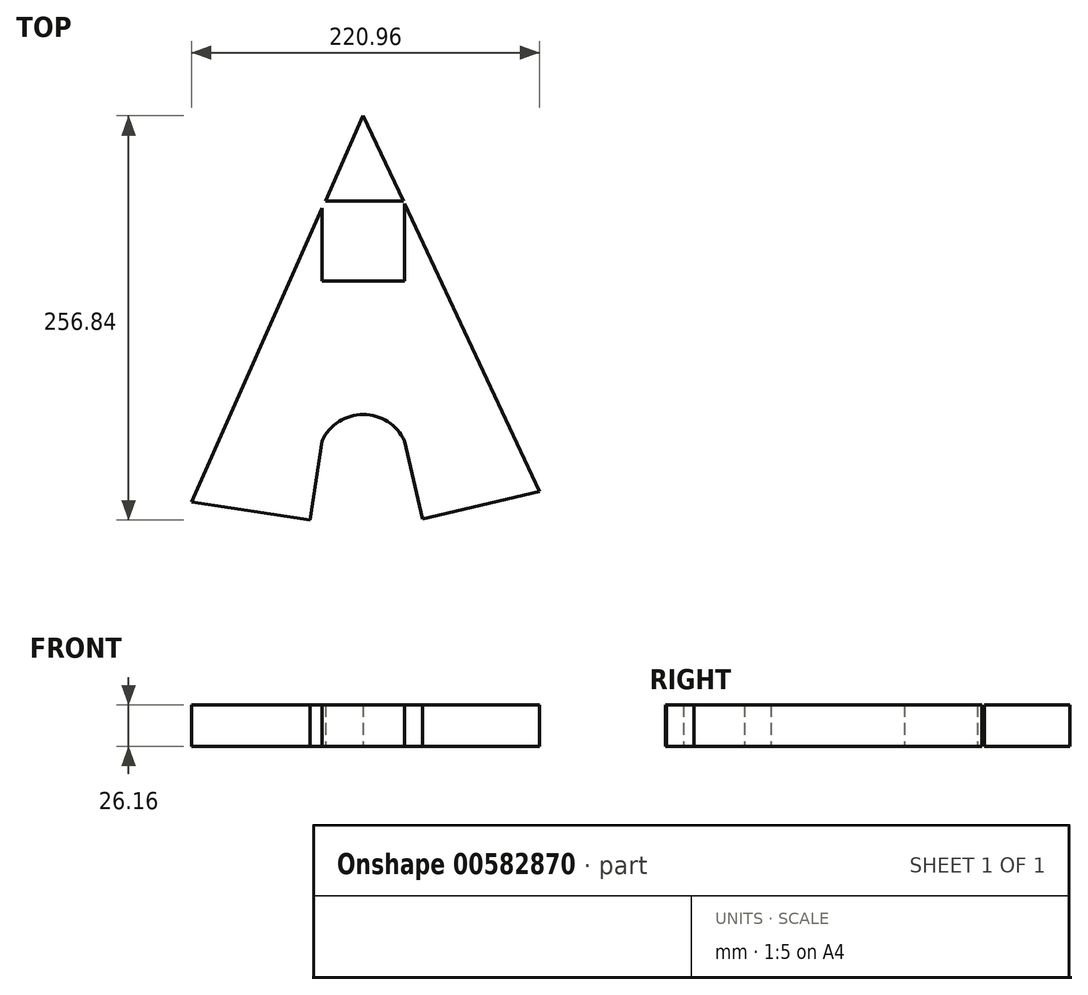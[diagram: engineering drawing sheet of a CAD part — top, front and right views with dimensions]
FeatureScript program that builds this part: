
annotation { "Feature Type Name" : "Feature", "Feature Type Description" : "" }
export const myFeature = defineFeature(function(context is Context, id is Id, definition is map)
    precondition{}
    {
        {
            var Q0;
            Q0=qCreatedBy(makeId("Top.planeOp"),FACE);
            var sketch = newSketch(context, id + "F0", { "sketchPlane" : qUnion([Q0])});
            skArc(sketch, "E0", {"start": v(52.24, 0) * mm, "mid": v(26.12, 16.74) * mm, "end": v(0, 0) * mm});
            skLineSegment(sketch, "E1", {"start": v(0, 0) * mm, "end": v(-7.57, -50.23) * mm});
            skLineSegment(sketch, "E2", {"start": v(0, 0) * mm, "end": v(0, 101.6) * mm});
            skLineSegment(sketch, "E3", {"start": v(52.24, 0) * mm, "end": v(63.87, -49.45) * mm});
            skLineSegment(sketch, "E4", {"start": v(52.24, 0) * mm, "end": v(52.24, 101.6) * mm});
            skLineSegment(sketch, "E5", {"start": v(52.24, 50.8) * mm, "end": v(0, 50.8) * mm});
            skLineSegment(sketch, "E6", {"start": v(0, 50.8) * mm, "end": v(52.24, 101.6) * mm});
            skLineSegment(sketch, "E7", {"start": v(0, 101.6) * mm, "end": v(52.24, 101.6) * mm});
            skLineSegment(sketch, "E8", {"start": v(0, 101.6) * mm, "end": v(52.24, 50.8) * mm});
            skLineSegment(sketch, "E9", {"start": v(0, 101.6) * mm, "end": v(0, 152.4) * mm});
            skLineSegment(sketch, "E10", {"start": v(0, 152.4) * mm, "end": v(52.24, 101.6) * mm});
            skLineSegment(sketch, "E11", {"start": v(0, 152.4) * mm, "end": v(52.24, 152.4) * mm});
            skLineSegment(sketch, "E12", {"start": v(52.24, 152.4) * mm, "end": v(52.24, 101.6) * mm});
            skLineSegment(sketch, "E13", {"start": v(52.24, 152.4) * mm, "end": v(0, 101.6) * mm});
            skLineSegment(sketch, "E14", {"start": v(0, 152.4) * mm, "end": v(26.12, 206.6) * mm});
            skPoint(sketch, "E14.endSnap0", {"position": v(26.12, 152.4) * mm});
            skLineSegment(sketch, "E15", {"start": v(26.12, 206.6) * mm, "end": v(52.24, 152.4) * mm});
            skLineSegment(sketch, "E16", {"start": v(-7.57, -50.23) * mm, "end": v(-82.92, -38.88) * mm});
            skLineSegment(sketch, "E17", {"start": v(-82.92, -38.88) * mm, "end": v(26.12, 206.6) * mm});
            skLineSegment(sketch, "E18", {"start": v(63.87, -49.45) * mm, "end": v(138.04, -32) * mm});
            skLineSegment(sketch, "E19", {"start": v(138.04, -32) * mm, "end": v(26.12, 206.6) * mm});
            skLineSegment(sketch, "E20", {"start": v(0, 30.06) * mm, "end": v(52.24, 30.06) * mm});
            skSolve(sketch);
        }
        {
            var Q0;
            {var subQ7=sQuery(id+"F0.wireOp",EDGE,"E1");Q0=makeQuery(id+"F0.imprint","IMPRINT",FACE,{"disambiguationData":[TD([[makeQuery(id+"F0.imprint","IMPRINT",EDGE,{"derivedFrom":subQ7}),-1.0]])]});}
            var Q1;
            {var subQ5=sQuery(id+"F0.wireOp",EDGE,"E3");Q1=makeQuery(id+"F0.imprint","IMPRINT",FACE,{"disambiguationData":[TD([[makeQuery(id+"F0.imprint","IMPRINT",EDGE,{"derivedFrom":subQ5}),1.0]])]});}
            var Q2;
            {var subQ0=sQuery(id+"F0.wireOp",EDGE,"E0");Q2=makeQuery(id+"F0.imprint","IMPRINT",FACE,{"disambiguationData":[TD([[makeQuery(id+"F0.imprint","IMPRINT",EDGE,{"derivedFrom":subQ0}),-1.0]])]});}
            var Q3;
            {var subQ0=sQuery(id+"F0.wireOp",EDGE,"E5");Q3=makeQuery(id+"F0.imprint","IMPRINT",FACE,{"disambiguationData":[TD([[makeQuery(id+"F0.imprint","IMPRINT",EDGE,{"derivedFrom":subQ0}),-1.0]])]});}
            var Q4;
            {var subQ0=sQuery(id+"F0.wireOp",EDGE,"E8");var subQ3=sQuery(id+"F0.wireOp",EDGE,"E6");var subQ5=makeQuery(id+"F0.imprint","INTERSECT",VERTEX,{"derivedFrom":[subQ3,subQ0]});Q4=makeQuery(id+"F0.imprint","IMPRINT",FACE,{"disambiguationData":[TD([[makeQuery(id+"F0.imprint","IMPRINT",EDGE,{"disambiguationData":[TD([[subQ5,1.0]])],"derivedFrom":subQ3}),1.0]])]});}
            var Q5;
            {var subQ0=sQuery(id+"F0.wireOp",EDGE,"E7");Q5=makeQuery(id+"F0.imprint","IMPRINT",FACE,{"disambiguationData":[TD([[makeQuery(id+"F0.imprint","IMPRINT",EDGE,{"derivedFrom":subQ0}),-1.0]])]});}
            var Q6;
            {var subQ0=sQuery(id+"F0.wireOp",EDGE,"E6");var subQ3=sQuery(id+"F0.wireOp",EDGE,"E8");var subQ5=makeQuery(id+"F0.imprint","INTERSECT",VERTEX,{"derivedFrom":[subQ0,subQ3]});Q6=makeQuery(id+"F0.imprint","IMPRINT",FACE,{"disambiguationData":[TD([[makeQuery(id+"F0.imprint","IMPRINT",EDGE,{"disambiguationData":[TD([[subQ5,-1.0]])],"derivedFrom":subQ3}),1.0]])]});}
            var Q7;
            {var subQ0=sQuery(id+"F0.wireOp",EDGE,"E17");var subQ1=sQuery(id+"F0.wireOp",EDGE,"E11");var subQ2=makeQuery(id+"F0.imprint","INTERSECT",VERTEX,{"derivedFrom":[subQ1,subQ0]});Q7=makeQuery(id+"F0.imprint","IMPRINT",FACE,{"disambiguationData":[TD([[makeQuery(id+"F0.imprint","IMPRINT",EDGE,{"disambiguationData":[TD([[subQ2,-1.0]])],"derivedFrom":subQ1}),1.0]])]});}
            var Q8;
            {var subQ0=sQuery(id+"F0.wireOp",EDGE,"E5");Q8=makeQuery(id+"F0.imprint","IMPRINT",FACE,{"disambiguationData":[TD([[makeQuery(id+"F0.imprint","IMPRINT",EDGE,{"derivedFrom":subQ0}),1.0]])]});}
            extrude(context, id + "F1", {"entities" : qUnion([Q0, Q1, Q2, Q3, Q4, Q5, Q6, Q7, Q8]), "depth" : 26.16 * mm, "offsetDistance" : 25.4 * mm});
        }
    });
